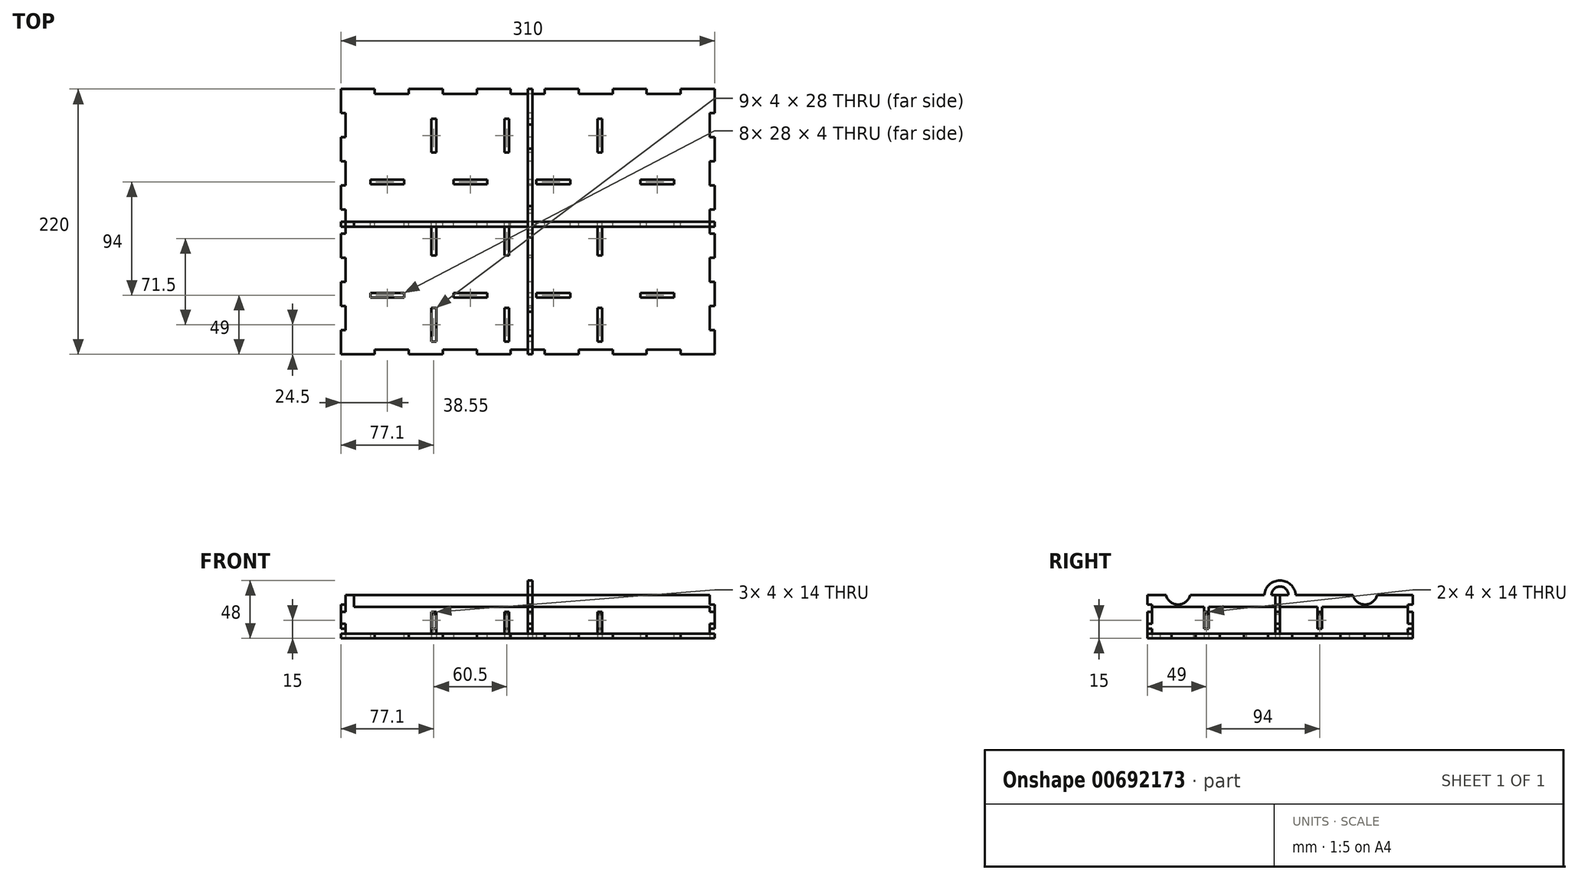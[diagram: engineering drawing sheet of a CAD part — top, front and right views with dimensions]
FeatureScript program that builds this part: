
annotation { "Feature Type Name" : "Feature", "Feature Type Description" : "" }
export const myFeature = defineFeature(function(context is Context, id is Id, definition is map)
    precondition{}
    {
        {
            var Q0;
            Q0=qCreatedBy(makeId("Top.planeOp"),FACE);
            var sketch = newSketch(context, id + "F0", { "sketchPlane" : qUnion([Q0])});
            skLineSegment(sketch, "E0", {"start": v(-155, 110) * mm, "end": v(-126.8, 110) * mm});
            skLineSegment(sketch, "E1", {"start": v(-126.8, 110) * mm, "end": v(-126.8, 106) * mm});
            skLineSegment(sketch, "E2", {"start": v(-126.8, 106) * mm, "end": v(-98.64, 106) * mm});
            skLineSegment(sketch, "E3", {"start": v(-155, 110) * mm, "end": v(-155, 90) * mm});
            skLineSegment(sketch, "E4", {"start": v(-155, 90) * mm, "end": v(-151, 90) * mm});
            skLineSegment(sketch, "E5", {"start": v(-151, 90) * mm, "end": v(-151, 70) * mm});
            skLineSegment(sketch, "E6", {"start": v(-151, 70) * mm, "end": v(-155, 70) * mm});
            skLineSegment(sketch, "E7", {"start": v(-98.64, 106) * mm, "end": v(-98.64, 110) * mm});
            skLineSegment(sketch, "E8.1.0.0", {"start": v(-98.64, 110) * mm, "end": v(-70.44, 110) * mm});
            skLineSegment(sketch, "E8.1.0.1", {"start": v(-70.44, 106) * mm, "end": v(-42.28, 106) * mm});
            skLineSegment(sketch, "E8.1.0.2", {"start": v(-42.28, 106) * mm, "end": v(-42.28, 110) * mm});
            skLineSegment(sketch, "E8.1.0.3", {"start": v(-70.44, 110) * mm, "end": v(-70.44, 106) * mm});
            skLineSegment(sketch, "E8.2.0.0", {"start": v(-42.28, 110) * mm, "end": v(-14.08, 110) * mm});
            skLineSegment(sketch, "E8.2.0.1", {"start": v(-14.08, 106) * mm, "end": v(14.08, 106) * mm});
            skLineSegment(sketch, "E8.2.0.2", {"start": v(14.08, 106) * mm, "end": v(14.08, 110) * mm});
            skLineSegment(sketch, "E8.2.0.3", {"start": v(-14.08, 110) * mm, "end": v(-14.08, 106) * mm});
            skLineSegment(sketch, "E8.3.0.0", {"start": v(14.08, 110) * mm, "end": v(42.28, 110) * mm});
            skLineSegment(sketch, "E8.3.0.1", {"start": v(42.28, 106) * mm, "end": v(70.44, 106) * mm});
            skLineSegment(sketch, "E8.3.0.2", {"start": v(70.44, 106) * mm, "end": v(70.44, 110) * mm});
            skLineSegment(sketch, "E8.3.0.3", {"start": v(42.28, 110) * mm, "end": v(42.28, 106) * mm});
            skLineSegment(sketch, "E8.4.0.0", {"start": v(70.44, 110) * mm, "end": v(98.64, 110) * mm});
            skLineSegment(sketch, "E8.4.0.1", {"start": v(98.64, 106) * mm, "end": v(126.8, 106) * mm});
            skLineSegment(sketch, "E8.4.0.2", {"start": v(126.8, 106) * mm, "end": v(126.8, 110) * mm});
            skLineSegment(sketch, "E8.4.0.3", {"start": v(98.64, 110) * mm, "end": v(98.64, 106) * mm});
            skLineSegment(sketch, "E8.5.0.0", {"start": v(126.8, 110) * mm, "end": v(155, 110) * mm});
            skLineSegment(sketch, "E8.direction1", {"start": v(-155, 110) * mm, "end": v(-98.64, 110) * mm, "construction": true});
            skLineSegment(sketch, "E9.0.1.0", {"start": v(-155, 70) * mm, "end": v(-155, 50) * mm});
            skLineSegment(sketch, "E9.0.1.1", {"start": v(-151, 50) * mm, "end": v(-151, 30) * mm});
            skLineSegment(sketch, "E9.0.1.2", {"start": v(-155, 50) * mm, "end": v(-151, 50) * mm});
            skLineSegment(sketch, "E9.0.1.3", {"start": v(-151, 30) * mm, "end": v(-155, 30) * mm});
            skLineSegment(sketch, "E9.0.2.0", {"start": v(-155, 30) * mm, "end": v(-155, 10) * mm});
            skLineSegment(sketch, "E9.0.2.1", {"start": v(-151, 10) * mm, "end": v(-151, -10) * mm});
            skLineSegment(sketch, "E9.0.2.2", {"start": v(-155, 10) * mm, "end": v(-151, 10) * mm});
            skLineSegment(sketch, "E9.0.2.3", {"start": v(-151, -10) * mm, "end": v(-155, -10) * mm});
            skLineSegment(sketch, "E9.0.3.0", {"start": v(-155, -10) * mm, "end": v(-155, -30) * mm});
            skLineSegment(sketch, "E9.0.3.1", {"start": v(-151, -30) * mm, "end": v(-151, -50) * mm});
            skLineSegment(sketch, "E9.0.3.2", {"start": v(-155, -30) * mm, "end": v(-151, -30) * mm});
            skLineSegment(sketch, "E9.0.3.3", {"start": v(-151, -50) * mm, "end": v(-155, -50) * mm});
            skLineSegment(sketch, "E9.0.4.0", {"start": v(-155, -50) * mm, "end": v(-155, -70) * mm});
            skLineSegment(sketch, "E9.0.4.1", {"start": v(-151, -70) * mm, "end": v(-151, -90) * mm});
            skLineSegment(sketch, "E9.0.4.2", {"start": v(-155, -70) * mm, "end": v(-151, -70) * mm});
            skLineSegment(sketch, "E9.0.4.3", {"start": v(-151, -90) * mm, "end": v(-155, -90) * mm});
            skLineSegment(sketch, "E9.0.5.0", {"start": v(-155, -90) * mm, "end": v(-155, -110) * mm});
            skLineSegment(sketch, "E9.direction1", {"start": v(-155, 70) * mm, "end": v(-124, 70) * mm, "construction": true});
            skLineSegment(sketch, "E9.direction2", {"start": v(-155, 70) * mm, "end": v(-155, 30) * mm, "construction": true});
            skLineSegment(sketch, "E10", {"start": v(155, 110) * mm, "end": v(155, 90) * mm});
            skLineSegment(sketch, "E11", {"start": v(155, 90) * mm, "end": v(151, 90) * mm});
            skLineSegment(sketch, "E12", {"start": v(151, 90) * mm, "end": v(151, 70) * mm});
            skLineSegment(sketch, "E13", {"start": v(151, 70) * mm, "end": v(155, 70) * mm});
            skLineSegment(sketch, "E14", {"start": v(-155, -110) * mm, "end": v(-126.8, -110) * mm});
            skLineSegment(sketch, "E15", {"start": v(-126.8, -110) * mm, "end": v(-126.8, -106) * mm});
            skLineSegment(sketch, "E16", {"start": v(-126.8, -106) * mm, "end": v(-98.64, -106) * mm});
            skLineSegment(sketch, "E17", {"start": v(-98.64, -106) * mm, "end": v(-98.64, -110) * mm});
            skLineSegment(sketch, "E18.1.0.0", {"start": v(-70.44, -106) * mm, "end": v(-42.28, -106) * mm});
            skLineSegment(sketch, "E18.1.0.1", {"start": v(-98.64, -110) * mm, "end": v(-70.44, -110) * mm});
            skLineSegment(sketch, "E18.1.0.2", {"start": v(-70.44, -110) * mm, "end": v(-70.44, -106) * mm});
            skLineSegment(sketch, "E18.1.0.3", {"start": v(-42.28, -106) * mm, "end": v(-42.28, -110) * mm});
            skLineSegment(sketch, "E18.2.0.0", {"start": v(-14.08, -106) * mm, "end": v(14.08, -106) * mm});
            skLineSegment(sketch, "E18.2.0.1", {"start": v(-42.28, -110) * mm, "end": v(-14.08, -110) * mm});
            skLineSegment(sketch, "E18.2.0.2", {"start": v(-14.08, -110) * mm, "end": v(-14.08, -106) * mm});
            skLineSegment(sketch, "E18.2.0.3", {"start": v(14.08, -106) * mm, "end": v(14.08, -110) * mm});
            skLineSegment(sketch, "E18.3.0.0", {"start": v(42.28, -106) * mm, "end": v(70.44, -106) * mm});
            skLineSegment(sketch, "E18.3.0.1", {"start": v(14.08, -110) * mm, "end": v(42.28, -110) * mm});
            skLineSegment(sketch, "E18.3.0.2", {"start": v(42.28, -110) * mm, "end": v(42.28, -106) * mm});
            skLineSegment(sketch, "E18.3.0.3", {"start": v(70.44, -106) * mm, "end": v(70.44, -110) * mm});
            skLineSegment(sketch, "E18.4.0.0", {"start": v(98.64, -106) * mm, "end": v(126.8, -106) * mm});
            skLineSegment(sketch, "E18.4.0.1", {"start": v(70.44, -110) * mm, "end": v(98.64, -110) * mm});
            skLineSegment(sketch, "E18.4.0.2", {"start": v(98.64, -110) * mm, "end": v(98.64, -106) * mm});
            skLineSegment(sketch, "E18.4.0.3", {"start": v(126.8, -106) * mm, "end": v(126.8, -110) * mm});
            skLineSegment(sketch, "E18.5.0.1", {"start": v(126.8, -110) * mm, "end": v(155, -110) * mm});
            skLineSegment(sketch, "E18.direction1", {"start": v(-155, -110) * mm, "end": v(-98.64, -110) * mm, "construction": true});
            skLineSegment(sketch, "E19.0.1.0", {"start": v(151, 50) * mm, "end": v(151, 30) * mm});
            skLineSegment(sketch, "E19.0.1.1", {"start": v(155, 70) * mm, "end": v(155, 50) * mm});
            skLineSegment(sketch, "E19.0.1.2", {"start": v(155, 50) * mm, "end": v(151, 50) * mm});
            skLineSegment(sketch, "E19.0.1.3", {"start": v(151, 30) * mm, "end": v(155, 30) * mm});
            skLineSegment(sketch, "E19.0.2.0", {"start": v(151, 10) * mm, "end": v(151, -10) * mm});
            skLineSegment(sketch, "E19.0.2.1", {"start": v(155, 30) * mm, "end": v(155, 10) * mm});
            skLineSegment(sketch, "E19.0.2.2", {"start": v(155, 10) * mm, "end": v(151, 10) * mm});
            skLineSegment(sketch, "E19.0.2.3", {"start": v(151, -10) * mm, "end": v(155, -10) * mm});
            skLineSegment(sketch, "E19.0.3.0", {"start": v(151, -30) * mm, "end": v(151, -50) * mm});
            skLineSegment(sketch, "E19.0.3.1", {"start": v(155, -10) * mm, "end": v(155, -30) * mm});
            skLineSegment(sketch, "E19.0.3.2", {"start": v(155, -30) * mm, "end": v(151, -30) * mm});
            skLineSegment(sketch, "E19.0.3.3", {"start": v(151, -50) * mm, "end": v(155, -50) * mm});
            skLineSegment(sketch, "E19.0.4.0", {"start": v(151, -70) * mm, "end": v(151, -90) * mm});
            skLineSegment(sketch, "E19.0.4.1", {"start": v(155, -50) * mm, "end": v(155, -70) * mm});
            skLineSegment(sketch, "E19.0.4.2", {"start": v(155, -70) * mm, "end": v(151, -70) * mm});
            skLineSegment(sketch, "E19.0.4.3", {"start": v(151, -90) * mm, "end": v(155, -90) * mm});
            skLineSegment(sketch, "E19.0.5.1", {"start": v(155, -90) * mm, "end": v(155, -110) * mm});
            skLineSegment(sketch, "E19.direction1", {"start": v(151, 70) * mm, "end": v(171.43, 70) * mm, "construction": true});
            skLineSegment(sketch, "E19.direction2", {"start": v(151, 70) * mm, "end": v(151, 30) * mm, "construction": true});
            skLineSegment(sketch, "E20", {"start": v(176.81, -61) * mm, "end": v(-206.45, -61) * mm, "construction": true});
            skLineSegment(sketch, "E21", {"start": v(220.81, 33) * mm, "end": v(-162.45, 33) * mm, "construction": true});
            skLineSegment(sketch, "E22", {"start": v(59.8, 157.7) * mm, "end": v(59.8, -215.6) * mm, "construction": true});
            skLineSegment(sketch, "E23", {"start": v(-17.4, 160.3) * mm, "end": v(-17.4, -213) * mm, "construction": true});
            skLineSegment(sketch, "E24", {"start": v(-77.9, 160.3) * mm, "end": v(-77.9, -213) * mm, "construction": true});
            skLineSegment(sketch, "E25.bottom", {"start": v(-15.4, 85.5) * mm, "end": v(-19.4, 85.5) * mm});
            skLineSegment(sketch, "E25.top", {"start": v(-15.4, 57.5) * mm, "end": v(-19.4, 57.5) * mm});
            skLineSegment(sketch, "E25.left", {"start": v(-15.4, 85.5) * mm, "end": v(-15.4, 57.5) * mm});
            skLineSegment(sketch, "E25.right", {"start": v(-19.4, 85.5) * mm, "end": v(-19.4, 57.5) * mm});
            skLineSegment(sketch, "E26.bottom", {"start": v(-15.4, 0) * mm, "end": v(-19.4, 0) * mm});
            skLineSegment(sketch, "E26.top", {"start": v(-15.4, -28) * mm, "end": v(-19.4, -28) * mm});
            skLineSegment(sketch, "E26.left", {"start": v(-15.4, 0) * mm, "end": v(-15.4, -28) * mm});
            skLineSegment(sketch, "E26.right", {"start": v(-19.4, 0) * mm, "end": v(-19.4, -28) * mm});
            skLineSegment(sketch, "E27.bottom", {"start": v(-15.4, -71.5) * mm, "end": v(-19.4, -71.5) * mm});
            skLineSegment(sketch, "E27.top", {"start": v(-15.4, -99.5) * mm, "end": v(-19.4, -99.5) * mm});
            skLineSegment(sketch, "E27.left", {"start": v(-15.4, -71.5) * mm, "end": v(-15.4, -99.5) * mm});
            skLineSegment(sketch, "E27.right", {"start": v(-19.4, -71.5) * mm, "end": v(-19.4, -99.5) * mm});
            skLineSegment(sketch, "E28.1.0.0", {"start": v(-75.9, 0) * mm, "end": v(-75.9, -28) * mm});
            skLineSegment(sketch, "E28.1.0.1", {"start": v(-79.9, 0) * mm, "end": v(-79.9, -28) * mm});
            skLineSegment(sketch, "E28.1.0.2", {"start": v(-75.9, -71.5) * mm, "end": v(-75.9, -99.5) * mm});
            skLineSegment(sketch, "E28.1.0.3", {"start": v(-75.9, 85.5) * mm, "end": v(-75.9, 57.5) * mm});
            skLineSegment(sketch, "E28.1.0.4", {"start": v(-79.9, -71.5) * mm, "end": v(-79.9, -99.5) * mm});
            skLineSegment(sketch, "E28.1.0.5", {"start": v(-79.9, 85.5) * mm, "end": v(-79.9, 57.5) * mm});
            skLineSegment(sketch, "E28.1.0.6", {"start": v(-75.9, -99.5) * mm, "end": v(-79.9, -99.5) * mm});
            skLineSegment(sketch, "E28.1.0.7", {"start": v(-75.9, -71.5) * mm, "end": v(-79.9, -71.5) * mm});
            skLineSegment(sketch, "E28.1.0.8", {"start": v(-75.9, 0) * mm, "end": v(-79.9, 0) * mm});
            skLineSegment(sketch, "E28.1.0.10", {"start": v(-75.9, -28) * mm, "end": v(-79.9, -28) * mm});
            skLineSegment(sketch, "E28.1.0.11", {"start": v(-75.9, 85.5) * mm, "end": v(-79.9, 85.5) * mm});
            skLineSegment(sketch, "E28.1.0.12", {"start": v(-75.9, 57.5) * mm, "end": v(-79.9, 57.5) * mm});
            skLineSegment(sketch, "E28.direction1", {"start": v(-19.4, -99.5) * mm, "end": v(-79.9, -99.5) * mm, "construction": true});
            skLineSegment(sketch, "E29.1.0.0", {"start": v(57.8, 0) * mm, "end": v(57.8, -28) * mm});
            skLineSegment(sketch, "E29.1.0.1", {"start": v(57.8, -71.5) * mm, "end": v(57.8, -99.5) * mm});
            skLineSegment(sketch, "E29.1.0.2", {"start": v(61.8, -71.5) * mm, "end": v(61.8, -99.5) * mm});
            skLineSegment(sketch, "E29.1.0.3", {"start": v(61.8, 0) * mm, "end": v(61.8, -28) * mm});
            skLineSegment(sketch, "E29.1.0.4", {"start": v(57.8, 85.5) * mm, "end": v(57.8, 57.5) * mm});
            skLineSegment(sketch, "E29.1.0.5", {"start": v(61.8, 85.5) * mm, "end": v(61.8, 57.5) * mm});
            skLineSegment(sketch, "E29.1.0.6", {"start": v(61.8, 85.5) * mm, "end": v(57.8, 85.5) * mm});
            skLineSegment(sketch, "E29.1.0.7", {"start": v(61.8, 57.5) * mm, "end": v(57.8, 57.5) * mm});
            skLineSegment(sketch, "E29.1.0.8", {"start": v(61.8, -71.5) * mm, "end": v(57.8, -71.5) * mm});
            skLineSegment(sketch, "E29.1.0.11", {"start": v(61.8, -28) * mm, "end": v(57.8, -28) * mm});
            skLineSegment(sketch, "E29.1.0.12", {"start": v(61.8, 0) * mm, "end": v(57.8, 0) * mm});
            skLineSegment(sketch, "E29.1.0.13", {"start": v(61.8, -99.5) * mm, "end": v(57.8, -99.5) * mm});
            skLineSegment(sketch, "E29.direction1", {"start": v(-19.4, -99.5) * mm, "end": v(57.8, -99.5) * mm, "construction": true});
            skLineSegment(sketch, "E30.bottom", {"start": v(121.4, 35) * mm, "end": v(93.4, 35) * mm});
            skLineSegment(sketch, "E30.top", {"start": v(121.4, 31) * mm, "end": v(93.4, 31) * mm});
            skLineSegment(sketch, "E30.left", {"start": v(121.4, 35) * mm, "end": v(121.4, 31) * mm});
            skLineSegment(sketch, "E30.right", {"start": v(93.4, 35) * mm, "end": v(93.4, 31) * mm});
            skLineSegment(sketch, "E31.bottom", {"start": v(35.2, 31) * mm, "end": v(7.2, 31) * mm});
            skLineSegment(sketch, "E31.top", {"start": v(35.2, 35) * mm, "end": v(7.2, 35) * mm});
            skLineSegment(sketch, "E31.left", {"start": v(35.2, 31) * mm, "end": v(35.2, 35) * mm});
            skLineSegment(sketch, "E31.right", {"start": v(7.2, 31) * mm, "end": v(7.2, 35) * mm});
            skLineSegment(sketch, "E32.bottom", {"start": v(-33.65, 35) * mm, "end": v(-61.65, 35) * mm});
            skLineSegment(sketch, "E32.top", {"start": v(-33.65, 31) * mm, "end": v(-61.65, 31) * mm});
            skLineSegment(sketch, "E32.left", {"start": v(-33.65, 35) * mm, "end": v(-33.65, 31) * mm});
            skLineSegment(sketch, "E32.right", {"start": v(-61.65, 35) * mm, "end": v(-61.65, 31) * mm});
            skLineSegment(sketch, "E33.bottom", {"start": v(-102.45, 31) * mm, "end": v(-130.45, 31) * mm});
            skLineSegment(sketch, "E33.top", {"start": v(-102.45, 35) * mm, "end": v(-130.45, 35) * mm});
            skLineSegment(sketch, "E33.left", {"start": v(-102.45, 31) * mm, "end": v(-102.45, 35) * mm});
            skLineSegment(sketch, "E33.right", {"start": v(-130.45, 31) * mm, "end": v(-130.45, 35) * mm});
            skLineSegment(sketch, "E34.0.1.0", {"start": v(-33.65, -59) * mm, "end": v(-61.65, -59) * mm});
            skLineSegment(sketch, "E34.0.1.1", {"start": v(-102.45, -59) * mm, "end": v(-130.45, -59) * mm});
            skLineSegment(sketch, "E34.0.1.2", {"start": v(35.2, -63) * mm, "end": v(7.2, -63) * mm});
            skLineSegment(sketch, "E34.0.1.3", {"start": v(121.4, -63) * mm, "end": v(93.4, -63) * mm});
            skLineSegment(sketch, "E34.0.1.4", {"start": v(35.2, -59) * mm, "end": v(7.2, -59) * mm});
            skLineSegment(sketch, "E34.0.1.5", {"start": v(121.4, -59) * mm, "end": v(93.4, -59) * mm});
            skLineSegment(sketch, "E34.0.1.6", {"start": v(-33.65, -63) * mm, "end": v(-61.65, -63) * mm});
            skLineSegment(sketch, "E34.0.1.7", {"start": v(-102.45, -63) * mm, "end": v(-130.45, -63) * mm});
            skLineSegment(sketch, "E34.0.1.8", {"start": v(35.2, -63) * mm, "end": v(35.2, -59) * mm});
            skLineSegment(sketch, "E34.0.1.9", {"start": v(121.4, -59) * mm, "end": v(121.4, -63) * mm});
            skLineSegment(sketch, "E34.0.1.10", {"start": v(93.4, -59) * mm, "end": v(93.4, -63) * mm});
            skLineSegment(sketch, "E34.0.1.11", {"start": v(-102.45, -63) * mm, "end": v(-102.45, -59) * mm});
            skLineSegment(sketch, "E34.0.1.12", {"start": v(-130.45, -63) * mm, "end": v(-130.45, -59) * mm});
            skLineSegment(sketch, "E34.0.1.13", {"start": v(7.2, -63) * mm, "end": v(7.2, -59) * mm});
            skLineSegment(sketch, "E34.0.1.14", {"start": v(-33.65, -59) * mm, "end": v(-33.65, -63) * mm});
            skLineSegment(sketch, "E34.0.1.15", {"start": v(-61.65, -59) * mm, "end": v(-61.65, -63) * mm});
            skLineSegment(sketch, "E34.direction1", {"start": v(-130.45, 31) * mm, "end": v(-110.22, 31) * mm, "construction": true});
            skLineSegment(sketch, "E34.direction2", {"start": v(-130.45, 31) * mm, "end": v(-130.45, -63) * mm, "construction": true});
            skSolve(sketch);
        }
        {
            var Q0;
            Q0=qSketchRegion(id+"F0",true);
            extrude(context, id + "F1", {"entities" : qUnion([Q0]), "depth" : 4 * mm});
        }
        {
            var Q0;
            Q0=qCreatedBy(makeId("Front.planeOp"),FACE);
            var sketch = newSketch(context, id + "F2", { "sketchPlane" : qUnion([Q0])});
            skLineSegment(sketch, "E35", {"start": v(-151, 26) * mm, "end": v(-151, 22) * mm});
            skLineSegment(sketch, "E36", {"start": v(-151, 22) * mm, "end": v(-155, 22) * mm});
            skLineSegment(sketch, "E37", {"start": v(-155, 22) * mm, "end": v(-155, 8) * mm});
            skLineSegment(sketch, "E38", {"start": v(-155, 8) * mm, "end": v(-151, 8) * mm});
            skLineSegment(sketch, "E39", {"start": v(-151, 8) * mm, "end": v(-151, 4) * mm});
            skLineSegment(sketch, "E40", {"start": v(151, 4) * mm, "end": v(151, 8) * mm});
            skLineSegment(sketch, "E41", {"start": v(151, 8) * mm, "end": v(155, 8) * mm});
            skLineSegment(sketch, "E42", {"start": v(155, 8) * mm, "end": v(155, 22) * mm});
            skLineSegment(sketch, "E43", {"start": v(155, 22) * mm, "end": v(151, 22) * mm});
            skLineSegment(sketch, "E44", {"start": v(151, 22) * mm, "end": v(151, 26) * mm});
            skLineSegment(sketch, "E45", {"start": v(151, 26) * mm, "end": v(-151, 26) * mm});
            skLineSegment(sketch, "E46", {"start": v(-151, 4) * mm, "end": v(-130.45, 4) * mm});
            skLineSegment(sketch, "E47", {"start": v(-130.45, 4) * mm, "end": v(-130.45, 0) * mm});
            skLineSegment(sketch, "E48", {"start": v(-130.45, 0) * mm, "end": v(-102.45, 0) * mm});
            skLineSegment(sketch, "E49", {"start": v(-102.45, 0) * mm, "end": v(-102.45, 4) * mm});
            skLineSegment(sketch, "E50", {"start": v(-61.65, 4) * mm, "end": v(-61.65, 0) * mm});
            skLineSegment(sketch, "E51", {"start": v(-61.65, 0) * mm, "end": v(-33.65, 0) * mm});
            skLineSegment(sketch, "E52", {"start": v(-33.65, 0) * mm, "end": v(-33.65, 4) * mm});
            skLineSegment(sketch, "E53", {"start": v(7.2, 4) * mm, "end": v(7.2, 0) * mm});
            skLineSegment(sketch, "E54", {"start": v(7.2, 0) * mm, "end": v(35.2, 0) * mm});
            skLineSegment(sketch, "E55", {"start": v(35.2, 0) * mm, "end": v(35.2, 4) * mm});
            skLineSegment(sketch, "E56", {"start": v(93.4, 4) * mm, "end": v(93.4, 0) * mm});
            skLineSegment(sketch, "E57", {"start": v(93.4, 0) * mm, "end": v(121.4, 0) * mm});
            skLineSegment(sketch, "E58", {"start": v(121.4, 0) * mm, "end": v(121.4, 4) * mm});
            skLineSegment(sketch, "E59", {"start": v(121.4, 4) * mm, "end": v(151, 4) * mm});
            skLineSegment(sketch, "E60", {"start": v(-79.9, 4) * mm, "end": v(-79.9, 20) * mm});
            skLineSegment(sketch, "E61", {"start": v(-79.9, 20) * mm, "end": v(-75.9, 20) * mm});
            skLineSegment(sketch, "E62", {"start": v(-75.9, 20) * mm, "end": v(-75.9, 4) * mm});
            skLineSegment(sketch, "E63", {"start": v(-75.9, 4) * mm, "end": v(-61.65, 4) * mm});
            skLineSegment(sketch, "E64", {"start": v(-79.9, 4) * mm, "end": v(-102.45, 4) * mm});
            skLineSegment(sketch, "E65", {"start": v(-33.65, 4) * mm, "end": v(-19.4, 4) * mm});
            skLineSegment(sketch, "E66", {"start": v(-19.4, 4) * mm, "end": v(-19.4, 20) * mm});
            skLineSegment(sketch, "E67", {"start": v(-19.4, 20) * mm, "end": v(-15.4, 20) * mm});
            skLineSegment(sketch, "E68", {"start": v(-15.4, 20) * mm, "end": v(-15.4, 4) * mm});
            skLineSegment(sketch, "E69", {"start": v(-15.4, 4) * mm, "end": v(7.2, 4) * mm});
            skLineSegment(sketch, "E70", {"start": v(35.2, 4) * mm, "end": v(57.8, 4) * mm});
            skLineSegment(sketch, "E71", {"start": v(57.8, 4) * mm, "end": v(57.8, 20) * mm});
            skLineSegment(sketch, "E72", {"start": v(57.8, 20) * mm, "end": v(61.8, 20) * mm});
            skLineSegment(sketch, "E73", {"start": v(61.8, 20) * mm, "end": v(61.8, 4) * mm});
            skLineSegment(sketch, "E74", {"start": v(61.8, 4) * mm, "end": v(93.4, 4) * mm});
            skLineSegment(sketch, "E75.bottom", {"start": v(-151, 26) * mm, "end": v(-144, 26) * mm});
            skLineSegment(sketch, "E75.top", {"start": v(-151, 36) * mm, "end": v(-144, 36) * mm});
            skLineSegment(sketch, "E75.left", {"start": v(-151, 26) * mm, "end": v(-151, 36) * mm});
            skLineSegment(sketch, "E75.right", {"start": v(-144, 26) * mm, "end": v(-144, 36) * mm});
            skSolve(sketch);
        }
        {
            var Q0;
            Q0=qSketchRegion(id+"F2",true);
            extrude(context, id + "F3", {"entities" : qUnion([Q0]), "depth" : 4 * mm});
        }
        {
            var Q0;
            Q0=qCreatedBy(makeId("Right.planeOp"),FACE);
            var sketch = newSketch(context, id + "F4", { "sketchPlane" : qUnion([Q0])});
            skLineSegment(sketch, "E76", {"start": v(-99.5, 4) * mm, "end": v(-99.5, 0) * mm});
            skLineSegment(sketch, "E77", {"start": v(-99.5, 0) * mm, "end": v(-71.5, 0) * mm});
            skLineSegment(sketch, "E78", {"start": v(-71.5, 0) * mm, "end": v(-71.5, 4) * mm});
            skLineSegment(sketch, "E79", {"start": v(-71.5, 4) * mm, "end": v(-28, 4) * mm});
            skLineSegment(sketch, "E80", {"start": v(-28, 4) * mm, "end": v(-28, 0) * mm});
            skLineSegment(sketch, "E81", {"start": v(-28, 0) * mm, "end": v(0, 0) * mm});
            skLineSegment(sketch, "E82", {"start": v(0, 0) * mm, "end": v(0, 4) * mm});
            skLineSegment(sketch, "E83", {"start": v(0, 4) * mm, "end": v(57.5, 4) * mm});
            skLineSegment(sketch, "E84", {"start": v(57.5, 4) * mm, "end": v(57.5, 0) * mm});
            skLineSegment(sketch, "E85", {"start": v(57.5, 0) * mm, "end": v(85.5, 0) * mm});
            skLineSegment(sketch, "E86", {"start": v(85.5, 0) * mm, "end": v(85.5, 4) * mm});
            skLineSegment(sketch, "E87", {"start": v(-99.5, 4) * mm, "end": v(-106, 4) * mm});
            skLineSegment(sketch, "E88", {"start": v(-106, 4) * mm, "end": v(-106, 8) * mm});
            skLineSegment(sketch, "E89", {"start": v(-106, 8) * mm, "end": v(-110, 8) * mm});
            skLineSegment(sketch, "E90", {"start": v(-110, 8) * mm, "end": v(-110, 22) * mm});
            skLineSegment(sketch, "E91", {"start": v(-110, 22) * mm, "end": v(-106, 22) * mm});
            skLineSegment(sketch, "E92", {"start": v(-106, 22) * mm, "end": v(-106, 26) * mm});
            skLineSegment(sketch, "E93", {"start": v(-106, 26) * mm, "end": v(-63, 26) * mm});
            skLineSegment(sketch, "E94", {"start": v(-59, 26) * mm, "end": v(31, 26) * mm});
            skLineSegment(sketch, "E95", {"start": v(106, 26) * mm, "end": v(106, 22) * mm});
            skLineSegment(sketch, "E96", {"start": v(106, 22) * mm, "end": v(110, 22) * mm});
            skLineSegment(sketch, "E97", {"start": v(110, 22) * mm, "end": v(110, 8) * mm});
            skLineSegment(sketch, "E98", {"start": v(110, 8) * mm, "end": v(106, 8) * mm});
            skLineSegment(sketch, "E99", {"start": v(106, 8) * mm, "end": v(106, 4) * mm});
            skLineSegment(sketch, "E100", {"start": v(106, 4) * mm, "end": v(85.5, 4) * mm});
            skLineSegment(sketch, "E101", {"start": v(-63, 26) * mm, "end": v(-63, 20) * mm});
            skLineSegment(sketch, "E102", {"start": v(-63, 20) * mm, "end": v(-59, 20) * mm});
            skLineSegment(sketch, "E103", {"start": v(-59, 20) * mm, "end": v(-59, 26) * mm});
            skLineSegment(sketch, "E104", {"start": v(31, 26) * mm, "end": v(31, 20) * mm});
            skLineSegment(sketch, "E105", {"start": v(31, 20) * mm, "end": v(35, 20) * mm});
            skLineSegment(sketch, "E106", {"start": v(35, 20) * mm, "end": v(35, 26) * mm});
            skLineSegment(sketch, "E107", {"start": v(35, 26) * mm, "end": v(106, 26) * mm});
            skSolve(sketch);
        }
        {
            var Q0;
            Q0=qSketchRegion(id+"F4",true);
            extrude(context, id + "F5", {"entities" : qUnion([Q0]), "depth" : 4 * mm});
        }
        {
            var Q0;
            Q0=qCreatedBy(makeId("Front.planeOp"),FACE);
            var sketch = newSketch(context, id + "F6", { "sketchPlane" : qUnion([Q0])});
            skLineSegment(sketch, "E108", {"start": v(-151, 36) * mm, "end": v(-151, 28) * mm});
            skLineSegment(sketch, "E109", {"start": v(-151, 28) * mm, "end": v(-155, 28) * mm});
            skLineSegment(sketch, "E110", {"start": v(-155, 28) * mm, "end": v(-155, 12) * mm});
            skLineSegment(sketch, "E111", {"start": v(-155, 12) * mm, "end": v(-151, 12) * mm});
            skLineSegment(sketch, "E112", {"start": v(-151, 12) * mm, "end": v(-151, 4) * mm});
            skLineSegment(sketch, "E113", {"start": v(-151, 4) * mm, "end": v(-126.8, 4) * mm});
            skLineSegment(sketch, "E114", {"start": v(-126.8, 4) * mm, "end": v(-126.8, 0) * mm});
            skLineSegment(sketch, "E115", {"start": v(-126.8, 0) * mm, "end": v(-98.64, 0) * mm});
            skLineSegment(sketch, "E116", {"start": v(-98.64, 0) * mm, "end": v(-98.64, 4) * mm});
            skLineSegment(sketch, "E117", {"start": v(-98.64, 4) * mm, "end": v(-70.44, 4) * mm});
            skLineSegment(sketch, "E118", {"start": v(-70.44, 4) * mm, "end": v(-70.44, 0) * mm});
            skLineSegment(sketch, "E119", {"start": v(-70.44, 0) * mm, "end": v(-42.28, 0) * mm});
            skLineSegment(sketch, "E120", {"start": v(-42.28, 0) * mm, "end": v(-42.28, 4) * mm});
            skLineSegment(sketch, "E121", {"start": v(-42.28, 4) * mm, "end": v(-14.08, 4) * mm});
            skLineSegment(sketch, "E122", {"start": v(-14.08, 4) * mm, "end": v(-14.08, 0) * mm});
            skLineSegment(sketch, "E123", {"start": v(42.28, 0) * mm, "end": v(42.28, 4) * mm});
            skLineSegment(sketch, "E124", {"start": v(14.08, 4) * mm, "end": v(42.28, 4) * mm});
            skLineSegment(sketch, "E125", {"start": v(14.08, 4) * mm, "end": v(14.08, 0) * mm});
            skLineSegment(sketch, "E126", {"start": v(70.44, 0) * mm, "end": v(70.44, 4) * mm});
            skLineSegment(sketch, "E127", {"start": v(70.44, 4) * mm, "end": v(98.64, 4) * mm});
            skLineSegment(sketch, "E128", {"start": v(98.64, 4) * mm, "end": v(98.64, 0) * mm});
            skLineSegment(sketch, "E129", {"start": v(98.64, 0) * mm, "end": v(126.8, 0) * mm});
            skLineSegment(sketch, "E130", {"start": v(126.8, 0) * mm, "end": v(126.8, 4) * mm});
            skLineSegment(sketch, "E131", {"start": v(126.8, 4) * mm, "end": v(151, 4) * mm});
            skLineSegment(sketch, "E132", {"start": v(151, 4) * mm, "end": v(151, 12) * mm});
            skLineSegment(sketch, "E133", {"start": v(151, 12) * mm, "end": v(155, 12) * mm});
            skLineSegment(sketch, "E134", {"start": v(155, 12) * mm, "end": v(155, 28) * mm});
            skLineSegment(sketch, "E135", {"start": v(155, 28) * mm, "end": v(151, 28) * mm});
            skLineSegment(sketch, "E136", {"start": v(151, 28) * mm, "end": v(151, 36) * mm});
            skLineSegment(sketch, "E137", {"start": v(151, 36) * mm, "end": v(-151, 36) * mm});
            skLineSegment(sketch, "E138", {"start": v(-14.08, 0) * mm, "end": v(14.08, 0) * mm});
            skLineSegment(sketch, "E139", {"start": v(42.28, 0) * mm, "end": v(70.44, 0) * mm});
            skLineSegment(sketch, "E140.bottom", {"start": v(-79.9, 22) * mm, "end": v(-75.9, 22) * mm});
            skLineSegment(sketch, "E140.top", {"start": v(-79.9, 8) * mm, "end": v(-75.9, 8) * mm});
            skLineSegment(sketch, "E140.left", {"start": v(-79.9, 22) * mm, "end": v(-79.9, 8) * mm});
            skLineSegment(sketch, "E140.right", {"start": v(-75.9, 22) * mm, "end": v(-75.9, 8) * mm});
            skLineSegment(sketch, "E141.bottom", {"start": v(-19.4, 22) * mm, "end": v(-15.4, 22) * mm});
            skLineSegment(sketch, "E141.top", {"start": v(-19.4, 8) * mm, "end": v(-15.4, 8) * mm});
            skLineSegment(sketch, "E141.left", {"start": v(-19.4, 22) * mm, "end": v(-19.4, 8) * mm});
            skLineSegment(sketch, "E141.right", {"start": v(-15.4, 22) * mm, "end": v(-15.4, 8) * mm});
            skLineSegment(sketch, "E142.bottom", {"start": v(57.8, 8) * mm, "end": v(61.8, 8) * mm});
            skLineSegment(sketch, "E142.top", {"start": v(57.8, 22) * mm, "end": v(61.8, 22) * mm});
            skLineSegment(sketch, "E142.left", {"start": v(57.8, 8) * mm, "end": v(57.8, 22) * mm});
            skLineSegment(sketch, "E142.right", {"start": v(61.8, 8) * mm, "end": v(61.8, 22) * mm});
            skSolve(sketch);
        }
        {
            var Q0;
            Q0=qSketchRegion(id+"F6",true);
            extrude(context, id + "F7", {"entities" : qUnion([Q0]), "depth" : 4 * mm});
        }
        {
            var Q0;
            Q0=qCreatedBy(makeId("Right.planeOp"),FACE);
            var sketch = newSketch(context, id + "F8", { "sketchPlane" : qUnion([Q0])});
            skLineSegment(sketch, "E143", {"start": v(-110, 12) * mm, "end": v(-106, 12) * mm});
            skLineSegment(sketch, "E144", {"start": v(-106, 12) * mm, "end": v(-106, 28) * mm});
            skLineSegment(sketch, "E145", {"start": v(-106, 28) * mm, "end": v(-110, 28) * mm});
            skLineSegment(sketch, "E146", {"start": v(-110, 28) * mm, "end": v(-110, 36) * mm});
            skLineSegment(sketch, "E147", {"start": v(-110, 36) * mm, "end": v(-94.5, 36) * mm});
            skLineSegment(sketch, "E148", {"start": v(-74.5, 36) * mm, "end": v(-13, 36) * mm});
            skLineSegment(sketch, "E149", {"start": v(13, 36) * mm, "end": v(60.5, 36) * mm});
            skLineSegment(sketch, "E150", {"start": v(80.5, 36) * mm, "end": v(110, 36) * mm});
            skLineSegment(sketch, "E151", {"start": v(110, 36) * mm, "end": v(110, 28) * mm});
            skLineSegment(sketch, "E152", {"start": v(110, 28) * mm, "end": v(106, 28) * mm});
            skLineSegment(sketch, "E153", {"start": v(106, 28) * mm, "end": v(106, 12) * mm});
            skLineSegment(sketch, "E154", {"start": v(106, 12) * mm, "end": v(110, 12) * mm});
            skLineSegment(sketch, "E155", {"start": v(-110, 12) * mm, "end": v(-110, 4) * mm});
            skLineSegment(sketch, "E156", {"start": v(-110, 4) * mm, "end": v(-90, 4) * mm});
            skLineSegment(sketch, "E157", {"start": v(-90, 4) * mm, "end": v(-90, 0) * mm});
            skLineSegment(sketch, "E158", {"start": v(-90, 0) * mm, "end": v(-70, 0) * mm});
            skLineSegment(sketch, "E159", {"start": v(-70, 0) * mm, "end": v(-70, 4) * mm});
            skLineSegment(sketch, "E160", {"start": v(-70, 4) * mm, "end": v(-50, 4) * mm});
            skLineSegment(sketch, "E161", {"start": v(-50, 4) * mm, "end": v(-50, 0) * mm});
            skLineSegment(sketch, "E162", {"start": v(-50, 0) * mm, "end": v(-30, 0) * mm});
            skLineSegment(sketch, "E163", {"start": v(-30, 0) * mm, "end": v(-30, 4) * mm});
            skLineSegment(sketch, "E164", {"start": v(-30, 4) * mm, "end": v(-10, 4) * mm});
            skLineSegment(sketch, "E165", {"start": v(-10, 4) * mm, "end": v(-10, 0) * mm});
            skLineSegment(sketch, "E166", {"start": v(-10, 0) * mm, "end": v(10, 0) * mm});
            skLineSegment(sketch, "E167", {"start": v(10, 0) * mm, "end": v(10, 4) * mm});
            skLineSegment(sketch, "E168", {"start": v(10, 4) * mm, "end": v(30, 4) * mm});
            skLineSegment(sketch, "E169", {"start": v(30, 4) * mm, "end": v(30, 0) * mm});
            skLineSegment(sketch, "E170", {"start": v(30, 0) * mm, "end": v(50, 0) * mm});
            skLineSegment(sketch, "E171", {"start": v(50, 0) * mm, "end": v(50, 4) * mm});
            skLineSegment(sketch, "E172", {"start": v(50, 4) * mm, "end": v(70, 4) * mm});
            skLineSegment(sketch, "E173", {"start": v(70, 4) * mm, "end": v(70, 0) * mm});
            skLineSegment(sketch, "E174", {"start": v(70, 0) * mm, "end": v(90, 0) * mm});
            skLineSegment(sketch, "E175", {"start": v(90, 0) * mm, "end": v(90, 4) * mm});
            skLineSegment(sketch, "E176", {"start": v(90, 4) * mm, "end": v(110, 4) * mm});
            skLineSegment(sketch, "E177", {"start": v(110, 4) * mm, "end": v(110, 12) * mm});
            skArc(sketch, "E178", {"start": v(13, 36) * mm, "mid": v(0, 48) * mm, "end": v(-13, 36) * mm});
            skLineSegment(sketch, "E179", {"start": v(-84.5, 48) * mm, "end": v(70.5, 48) * mm, "construction": true});
            skArc(sketch, "E180", {"start": v(-94.5, 36) * mm, "mid": v(-84.5, 28) * mm, "end": v(-74.5, 36) * mm});
            skArc(sketch, "E181", {"start": v(60.5, 36) * mm, "mid": v(70.5, 28) * mm, "end": v(80.5, 36) * mm});
            skLineSegment(sketch, "E182", {"start": v(-84.5, 28) * mm, "end": v(70.5, 28) * mm, "construction": true});
            skLineSegment(sketch, "E183", {"start": v(-84.5, 38.25) * mm, "end": v(-84.5, 28) * mm, "construction": true});
            skLineSegment(sketch, "E184", {"start": v(70.5, 38.25) * mm, "end": v(70.5, 28) * mm, "construction": true});
            skLineSegment(sketch, "E185.bottom", {"start": v(-63, 8) * mm, "end": v(-59, 8) * mm});
            skLineSegment(sketch, "E185.top", {"start": v(-63, 22) * mm, "end": v(-59, 22) * mm});
            skLineSegment(sketch, "E185.left", {"start": v(-63, 8) * mm, "end": v(-63, 22) * mm});
            skLineSegment(sketch, "E185.right", {"start": v(-59, 8) * mm, "end": v(-59, 22) * mm});
            skLineSegment(sketch, "E186.bottom", {"start": v(31, 8) * mm, "end": v(35, 8) * mm});
            skLineSegment(sketch, "E186.top", {"start": v(31, 22) * mm, "end": v(35, 22) * mm});
            skLineSegment(sketch, "E186.left", {"start": v(31, 8) * mm, "end": v(31, 22) * mm});
            skLineSegment(sketch, "E186.right", {"start": v(35, 8) * mm, "end": v(35, 22) * mm});
            skLineSegment(sketch, "E187", {"start": v(-7, 36) * mm, "end": v(7, 36) * mm});
            skArc(sketch, "E188", {"start": v(7, 36) * mm, "mid": v(0, 43) * mm, "end": v(-7, 36) * mm});
            skLineSegment(sketch, "E189", {"start": v(35, 22) * mm, "end": v(70.5, 22) * mm, "construction": true});
            skLineSegment(sketch, "E190", {"start": v(70.5, 22) * mm, "end": v(106, 22) * mm, "construction": true});
            skLineSegment(sketch, "E191", {"start": v(-63, 22) * mm, "end": v(-84.5, 22) * mm, "construction": true});
            skLineSegment(sketch, "E192", {"start": v(-84.5, 22) * mm, "end": v(-106, 22) * mm, "construction": true});
            skLineSegment(sketch, "E193", {"start": v(-13, 36) * mm, "end": v(-7, 36) * mm, "construction": true});
            skLineSegment(sketch, "E194", {"start": v(7, 36) * mm, "end": v(13, 36) * mm, "construction": true});
            skSolve(sketch);
        }
        {
            var Q0;
            Q0=qSketchRegion(id+"F8",true);
            extrude(context, id + "F9", {"entities" : qUnion([Q0]), "depth" : 4 * mm});
        }
    });
